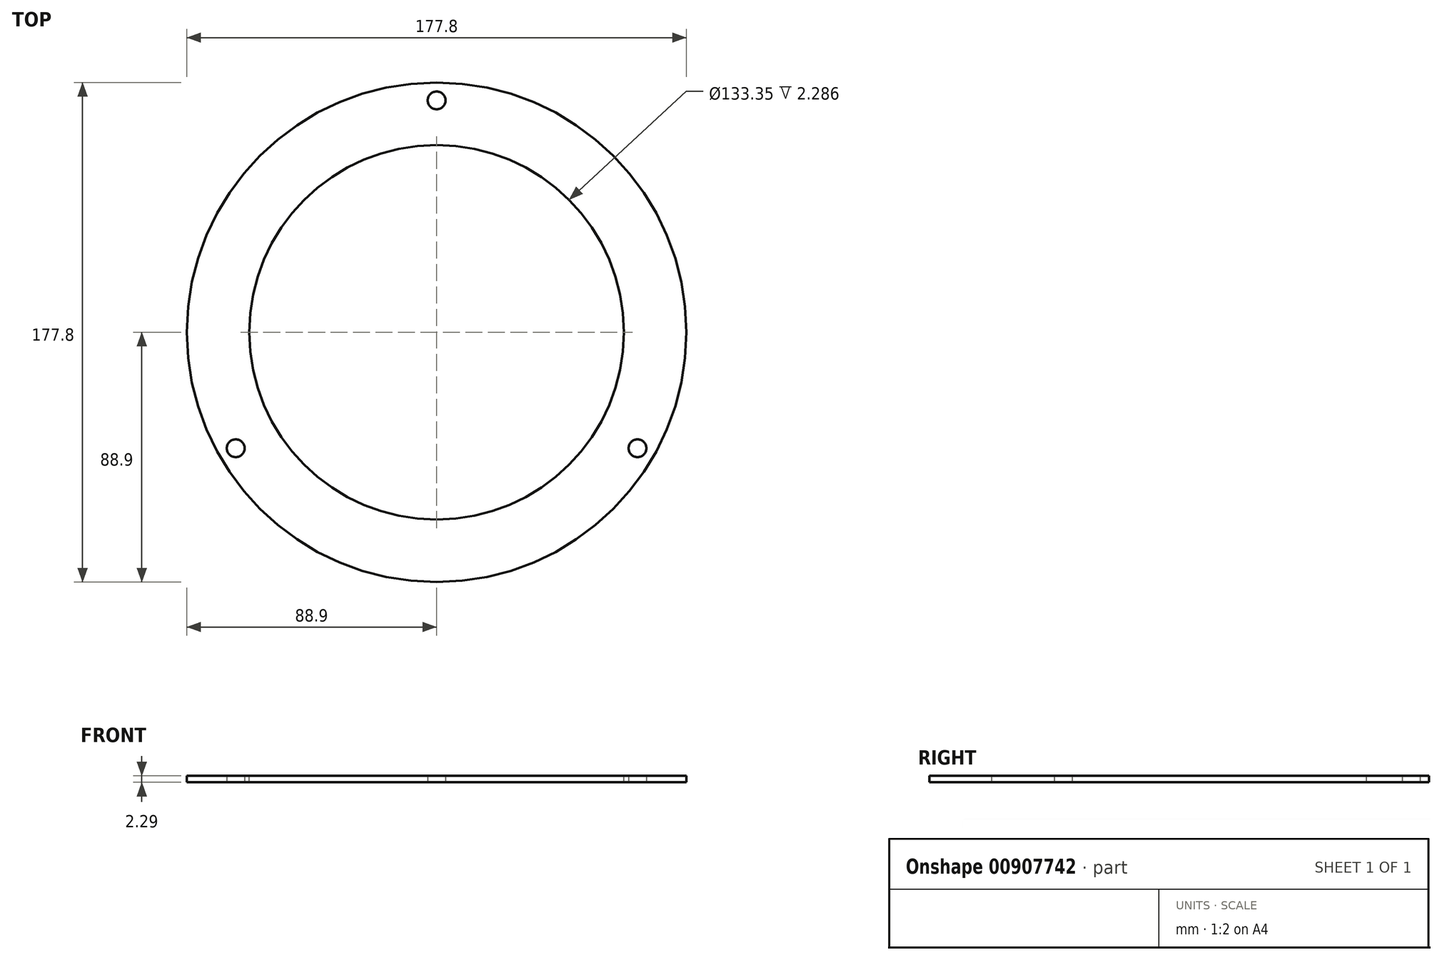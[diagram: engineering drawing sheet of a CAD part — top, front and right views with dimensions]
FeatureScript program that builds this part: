
annotation { "Feature Type Name" : "Feature", "Feature Type Description" : "" }
export const myFeature = defineFeature(function(context is Context, id is Id, definition is map)
    precondition{}
    {
        {
            var Q0;
            Q0=qCreatedBy(makeId("Top.planeOp"),FACE);
            var sketch = newSketch(context, id + "F0", { "sketchPlane" : qUnion([Q0])});
            skCircle(sketch, "E0", {"center": v(0, 0) * mm, "radius": 88.9 * mm});
            skCircle(sketch, "E1", {"center": v(0, 82.55) * mm, "radius": 3.18 * mm});
            skCircle(sketch, "E2.1.0", {"center": v(-71.5, -41.27) * mm, "radius": 3.18 * mm});
            skCircle(sketch, "E2.2.0", {"center": v(71.5, -41.27) * mm, "radius": 3.18 * mm});
            skSolve(sketch);
        }
        {
            var Q0;
            Q0=makeQuery(id+"F0.imprint","IMPRINT",FACE,{"disambiguationData":[TD([[makeQuery(id+"F0.imprint","IMPRINT",EDGE,{"derivedFrom":sQuery(id+"F0.wireOp",EDGE,"E0")}),1.0]])]});
            extrude(context, id + "F1", {"entities" : qUnion([Q0]), "depth" : 2.3 * mm, "offsetDistance" : 25.4 * mm});
        }
        {
            var Q0;
            Q0=makeQuery(id+"F1.opExtrude","CAP_FACE",FACE,{"disambiguationData":[OSD([sQuery(id+"F0.wireOp",EDGE,"E0"),sQuery(id+"F0.wireOp",EDGE,"E1"),sQuery(id+"F0.wireOp",EDGE,"E2.1.0"),sQuery(id+"F0.wireOp",EDGE,"E2.2.0")])],"isStart":false});
            var sketch = newSketch(context, id + "F2", { "sketchPlane" : qUnion([Q0])});
            skCircle(sketch, "E3", {"center": v(0, 0) * mm, "radius": 66.68 * mm});
            skSolve(sketch);
        }
        {
            var Q0;
            Q0=makeQuery(id+"F2.imprint","IMPRINT",FACE,{"disambiguationData":[TD([[makeQuery(id+"F2.imprint","IMPRINT",EDGE,{"derivedFrom":sQuery(id+"F2.wireOp",EDGE,"E3")}),1.0]])]});
            extrude(context, id + "F3", {"entities" : qUnion([Q0]), "operationType" : NewBodyOperationType.REMOVE, "oppositeDirection" : true, "depth" : 25.4 * mm, "offsetDistance" : 25.4 * mm});
        }
    });
